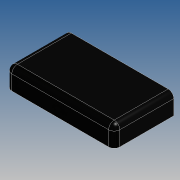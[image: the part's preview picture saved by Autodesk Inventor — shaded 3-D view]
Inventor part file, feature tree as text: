
AUTODESK INVENTOR PART (.ipt)
format: ipt  version: 2015 SP1 (Build 190203100, 203)  size: 278,016 bytes
history: native  units: mm
features: extrude x3, fillet x3, sketch x3, shell x1, chamfer x1, mirror x1, projected_geometry x1
ambient origin geometry x8: Origin, YZ Plane, XZ Plane, XY Plane, X Axis, Y Axis, Z Axis, Center Point
bodies: Solid1 (feature_tree)
feature tree (13):
  extrude  "Extrusion1"  Depth=32.0mm
  fillet  "Fillet1"  Radius=11.0mm
  fillet  "Fillet2"  Radius=2.0mm
  shell  "Shell1"  Thickness=3.0mm
  extrude  "Extrusion3"  Depth=1.0mm
  extrude  "Extrusion4"  Depth=0.2mm
  chamfer  "Chamfer2"  Distance=0.2mm
  fillet  "Fillet4"  Radius=0.2mm
  mirror  "Mirror1"
  sketch  "Sketch1"  dims[d0=29.0mm d1=32.0mm d2=11.0mm d3=0.0mm d4=2.0mm d5=3.0mm]
  sketch  "Sketch3"  dims[d6=3.0mm d19=1.0mm]
  sketch  "Sketch4"  dims[d20=2.0mm d21=0.0mm d22=5.0mm d23=0.2mm d24=0.2mm d25=10.0mm d26=10.0mm d27=3.0mm d28=0.4mm d29=0.8mm d30=0.0mm d32=0.4mm d33=2.0mm d34=45.0deg d35=0.2mm]
  projected_geometry  "Project Cut Edges1"
